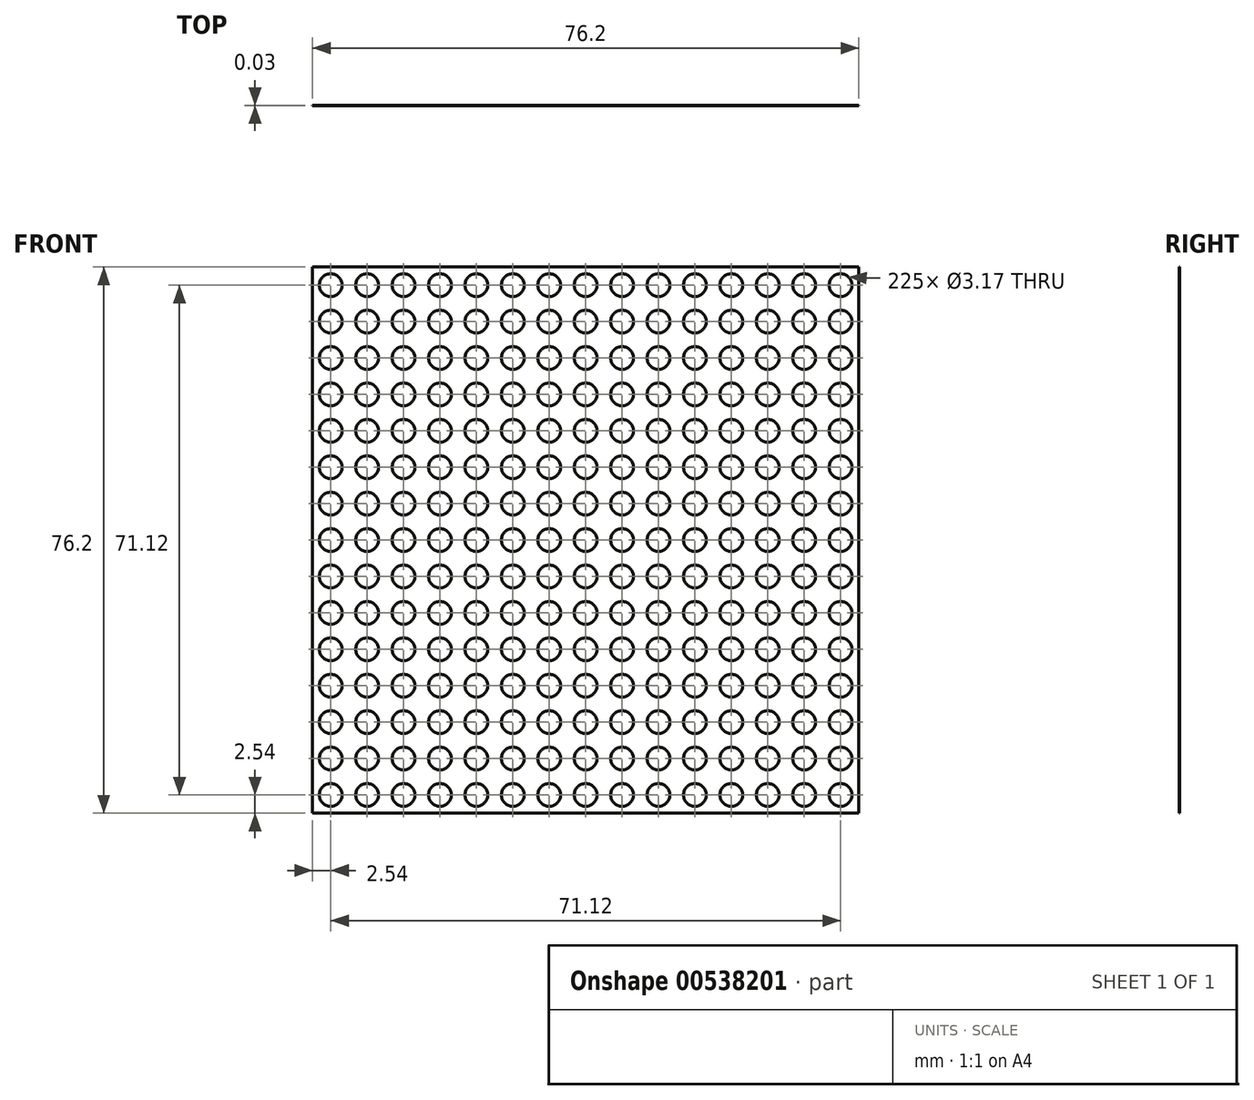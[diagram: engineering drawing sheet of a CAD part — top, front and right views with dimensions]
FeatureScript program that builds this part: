
annotation { "Feature Type Name" : "Feature", "Feature Type Description" : "" }
export const myFeature = defineFeature(function(context is Context, id is Id, definition is map)
    precondition{}
    {
        {
            var Q0;
            Q0=qCreatedBy(makeId("Front.planeOp"),FACE);
            var sketch = newSketch(context, id + "F0", { "sketchPlane" : qUnion([Q0])});
            skLineSegment(sketch, "E0", {"start": v(0, 0) * mm, "end": v(5.08, 0) * mm});
            skLineSegment(sketch, "E1", {"start": v(0, 5.08) * mm, "end": v(0, 0) * mm});
            skPoint(sketch, "E2", {"position": v(2.54, 2.54) * mm});
            skCircle(sketch, "E3", {"center": v(2.54, 2.54) * mm, "radius": 1.58 * mm});
            skPoint(sketch, "E4.MirrorP", {"position": v(7.62, 2.54) * mm});
            skCircle(sketch, "E5.MirrorC", {"center": v(7.62, 2.54) * mm, "radius": 1.58 * mm});
            skLineSegment(sketch, "E6.MirrorCS", {"start": v(10.16, 0) * mm, "end": v(5.08, 0) * mm});
            skCircle(sketch, "E7.MirrorC", {"center": v(17.78, 2.54) * mm, "radius": 1.58 * mm});
            skLineSegment(sketch, "E8.MirrorCS", {"start": v(20.32, 0) * mm, "end": v(15.24, 0) * mm});
            skCircle(sketch, "E9.MirrorC", {"center": v(12.7, 2.54) * mm, "radius": 1.58 * mm});
            skLineSegment(sketch, "E10.MirrorCS", {"start": v(10.16, 0) * mm, "end": v(15.24, 0) * mm});
            skPoint(sketch, "E11.MirrorP", {"position": v(33.02, 2.54) * mm});
            skPoint(sketch, "E12.MirrorP", {"position": v(38.1, 2.54) * mm});
            skCircle(sketch, "E13.MirrorC", {"center": v(38.1, 2.54) * mm, "radius": 1.58 * mm});
            skLineSegment(sketch, "E14.MirrorCS", {"start": v(40.64, 0) * mm, "end": v(35.56, 0) * mm});
            skLineSegment(sketch, "E15.MirrorCS", {"start": v(20.32, 0) * mm, "end": v(25.4, 0) * mm});
            skCircle(sketch, "E16.MirrorC", {"center": v(33.02, 2.54) * mm, "radius": 1.58 * mm});
            skLineSegment(sketch, "E17.MirrorCS", {"start": v(30.48, 0) * mm, "end": v(25.4, 0) * mm});
            skPoint(sketch, "E18.MirrorP", {"position": v(22.86, 2.54) * mm});
            skCircle(sketch, "E19.MirrorC", {"center": v(27.94, 2.54) * mm, "radius": 1.58 * mm});
            skCircle(sketch, "E20.MirrorC", {"center": v(22.86, 2.54) * mm, "radius": 1.58 * mm});
            skLineSegment(sketch, "E21.MirrorCS", {"start": v(30.48, 0) * mm, "end": v(35.56, 0) * mm});
            skPoint(sketch, "E22.MirrorP", {"position": v(43.18, 2.54) * mm});
            skPoint(sketch, "E23.MirrorP", {"position": v(73.66, 2.54) * mm});
            skCircle(sketch, "E24.MirrorC", {"center": v(43.18, 2.54) * mm, "radius": 1.58 * mm});
            skCircle(sketch, "E25.MirrorC", {"center": v(73.66, 2.54) * mm, "radius": 1.58 * mm});
            skCircle(sketch, "E26.MirrorC", {"center": v(63.5, 2.54) * mm, "radius": 1.58 * mm});
            skCircle(sketch, "E27.MirrorC", {"center": v(68.58, 2.54) * mm, "radius": 1.58 * mm});
            skLineSegment(sketch, "E28.MirrorCS", {"start": v(60.96, 0) * mm, "end": v(66.04, 0) * mm});
            skLineSegment(sketch, "E29.MirrorCS", {"start": v(50.8, 0) * mm, "end": v(55.88, 0) * mm});
            skPoint(sketch, "E30.MirrorP", {"position": v(58.42, 2.54) * mm});
            skLineSegment(sketch, "E31.MirrorCS", {"start": v(71.12, 0) * mm, "end": v(76.2, 0) * mm});
            skLineSegment(sketch, "E32.MirrorCS", {"start": v(60.96, 0) * mm, "end": v(55.88, 0) * mm});
            skLineSegment(sketch, "E33.MirrorCS", {"start": v(50.8, 0) * mm, "end": v(45.72, 0) * mm});
            skCircle(sketch, "E34.MirrorC", {"center": v(53.34, 2.54) * mm, "radius": 1.58 * mm});
            skLineSegment(sketch, "E35.MirrorCS", {"start": v(71.12, 0) * mm, "end": v(66.04, 0) * mm});
            skLineSegment(sketch, "E36.MirrorCS", {"start": v(40.64, 0) * mm, "end": v(45.72, 0) * mm});
            skPoint(sketch, "E37.MirrorP", {"position": v(48.26, 2.54) * mm});
            skCircle(sketch, "E38.MirrorC", {"center": v(48.26, 2.54) * mm, "radius": 1.58 * mm});
            skCircle(sketch, "E39.MirrorC", {"center": v(58.42, 2.54) * mm, "radius": 1.58 * mm});
            skLineSegment(sketch, "E40", {"start": v(76.2, 5.08) * mm, "end": v(76.2, 0) * mm});
            skPoint(sketch, "E41.MirrorP", {"position": v(12.7, 7.62) * mm});
            skCircle(sketch, "E42.MirrorC", {"center": v(53.34, 7.62) * mm, "radius": 1.58 * mm});
            skCircle(sketch, "E43.MirrorC", {"center": v(63.5, 7.62) * mm, "radius": 1.58 * mm});
            skCircle(sketch, "E44.MirrorC", {"center": v(33.02, 7.62) * mm, "radius": 1.58 * mm});
            skPoint(sketch, "E45.MirrorP", {"position": v(68.58, 7.62) * mm});
            skPoint(sketch, "E46.MirrorP", {"position": v(38.1, 7.62) * mm});
            skPoint(sketch, "E47.MirrorP", {"position": v(22.86, 7.62) * mm});
            skPoint(sketch, "E48.MirrorP", {"position": v(73.66, 7.62) * mm});
            skLineSegment(sketch, "E49.MirrorCS", {"start": v(76.2, 5.08) * mm, "end": v(76.2, 10.16) * mm});
            skCircle(sketch, "E50.MirrorC", {"center": v(48.26, 7.62) * mm, "radius": 1.58 * mm});
            skCircle(sketch, "E51.MirrorC", {"center": v(58.42, 7.62) * mm, "radius": 1.58 * mm});
            skCircle(sketch, "E52.MirrorC", {"center": v(68.58, 7.62) * mm, "radius": 1.58 * mm});
            skCircle(sketch, "E53.MirrorC", {"center": v(22.86, 7.62) * mm, "radius": 1.58 * mm});
            skCircle(sketch, "E54.MirrorC", {"center": v(27.94, 7.62) * mm, "radius": 1.58 * mm});
            skCircle(sketch, "E55.MirrorC", {"center": v(38.1, 7.62) * mm, "radius": 1.58 * mm});
            skPoint(sketch, "E56.MirrorP", {"position": v(17.78, 7.62) * mm});
            skCircle(sketch, "E57.MirrorC", {"center": v(73.66, 7.62) * mm, "radius": 1.58 * mm});
            skPoint(sketch, "E58.MirrorP", {"position": v(7.62, 7.62) * mm});
            skPoint(sketch, "E59.MirrorP", {"position": v(43.18, 7.62) * mm});
            skCircle(sketch, "E60.MirrorC", {"center": v(43.18, 7.62) * mm, "radius": 1.58 * mm});
            skCircle(sketch, "E61.MirrorC", {"center": v(12.7, 7.62) * mm, "radius": 1.58 * mm});
            skCircle(sketch, "E62.MirrorC", {"center": v(17.78, 7.62) * mm, "radius": 1.58 * mm});
            skPoint(sketch, "E63.MirrorP", {"position": v(2.54, 7.62) * mm});
            skCircle(sketch, "E64.MirrorC", {"center": v(7.62, 7.62) * mm, "radius": 1.58 * mm});
            skCircle(sketch, "E65.MirrorC", {"center": v(2.54, 7.62) * mm, "radius": 1.58 * mm});
            skLineSegment(sketch, "E66", {"start": v(0, 10.16) * mm, "end": v(0, 5.08) * mm});
            skPoint(sketch, "E67.MirrorP", {"position": v(2.54, 12.7) * mm});
            skCircle(sketch, "E68.MirrorC", {"center": v(2.54, 12.7) * mm, "radius": 1.58 * mm});
            skPoint(sketch, "E69.MirrorP", {"position": v(27.94, 17.78) * mm});
            skPoint(sketch, "E70.MirrorP", {"position": v(33.02, 17.78) * mm});
            skCircle(sketch, "E71.MirrorC", {"center": v(12.7, 12.7) * mm, "radius": 1.58 * mm});
            skPoint(sketch, "E72.MirrorP", {"position": v(2.54, 17.78) * mm});
            skLineSegment(sketch, "E73.MirrorCS", {"start": v(76.2, 15.24) * mm, "end": v(76.2, 10.16) * mm});
            skCircle(sketch, "E74.MirrorC", {"center": v(43.18, 12.7) * mm, "radius": 1.58 * mm});
            skCircle(sketch, "E75.MirrorC", {"center": v(2.54, 17.78) * mm, "radius": 1.58 * mm});
            skPoint(sketch, "E76.MirrorP", {"position": v(68.58, 17.78) * mm});
            skCircle(sketch, "E77.MirrorC", {"center": v(22.86, 12.7) * mm, "radius": 1.58 * mm});
            skPoint(sketch, "E78.MirrorP", {"position": v(58.42, 17.78) * mm});
            skPoint(sketch, "E79.MirrorP", {"position": v(73.66, 17.78) * mm});
            skPoint(sketch, "E80.MirrorP", {"position": v(73.66, 12.7) * mm});
            skLineSegment(sketch, "E81.MirrorCS", {"start": v(0, 15.24) * mm, "end": v(0, 20.32) * mm});
            skPoint(sketch, "E82.MirrorP", {"position": v(17.78, 17.78) * mm});
            skCircle(sketch, "E83.MirrorC", {"center": v(53.34, 17.78) * mm, "radius": 1.58 * mm});
            skCircle(sketch, "E84.MirrorC", {"center": v(63.5, 12.7) * mm, "radius": 1.58 * mm});
            skCircle(sketch, "E85.MirrorC", {"center": v(58.42, 17.78) * mm, "radius": 1.58 * mm});
            skPoint(sketch, "E86.MirrorP", {"position": v(7.62, 17.78) * mm});
            skCircle(sketch, "E87.MirrorC", {"center": v(63.5, 17.78) * mm, "radius": 1.58 * mm});
            skPoint(sketch, "E88.MirrorP", {"position": v(53.34, 12.7) * mm});
            skCircle(sketch, "E89.MirrorC", {"center": v(27.94, 17.78) * mm, "radius": 1.58 * mm});
            skPoint(sketch, "E90.MirrorP", {"position": v(48.26, 17.78) * mm});
            skCircle(sketch, "E91.MirrorC", {"center": v(58.42, 12.7) * mm, "radius": 1.58 * mm});
            skPoint(sketch, "E92.MirrorP", {"position": v(27.94, 12.7) * mm});
            skPoint(sketch, "E93.MirrorP", {"position": v(38.1, 17.78) * mm});
            skPoint(sketch, "E94.MirrorP", {"position": v(43.18, 17.78) * mm});
            skCircle(sketch, "E95.MirrorC", {"center": v(68.58, 12.7) * mm, "radius": 1.58 * mm});
            skCircle(sketch, "E96.MirrorC", {"center": v(68.58, 17.78) * mm, "radius": 1.58 * mm});
            skCircle(sketch, "E97.MirrorC", {"center": v(22.86, 17.78) * mm, "radius": 1.58 * mm});
            skPoint(sketch, "E98.MirrorP", {"position": v(12.7, 17.78) * mm});
            skCircle(sketch, "E99.MirrorC", {"center": v(27.94, 12.7) * mm, "radius": 1.58 * mm});
            skPoint(sketch, "E100.MirrorP", {"position": v(7.62, 12.7) * mm});
            skPoint(sketch, "E101.MirrorP", {"position": v(48.26, 12.7) * mm});
            skCircle(sketch, "E102.MirrorC", {"center": v(48.26, 17.78) * mm, "radius": 1.58 * mm});
            skPoint(sketch, "E103.MirrorP", {"position": v(33.02, 12.7) * mm});
            skCircle(sketch, "E104.MirrorC", {"center": v(33.02, 12.7) * mm, "radius": 1.58 * mm});
            skCircle(sketch, "E105.MirrorC", {"center": v(38.1, 12.7) * mm, "radius": 1.58 * mm});
            skLineSegment(sketch, "E106.MirrorCS", {"start": v(0, 10.16) * mm, "end": v(0, 15.24) * mm});
            skLineSegment(sketch, "E107.MirrorCS", {"start": v(76.2, 15.24) * mm, "end": v(76.2, 20.32) * mm});
            skCircle(sketch, "E108.MirrorC", {"center": v(7.62, 17.78) * mm, "radius": 1.58 * mm});
            skCircle(sketch, "E109.MirrorC", {"center": v(17.78, 17.78) * mm, "radius": 1.58 * mm});
            skCircle(sketch, "E110.MirrorC", {"center": v(12.7, 17.78) * mm, "radius": 1.58 * mm});
            skCircle(sketch, "E111.MirrorC", {"center": v(38.1, 17.78) * mm, "radius": 1.58 * mm});
            skCircle(sketch, "E112.MirrorC", {"center": v(33.02, 17.78) * mm, "radius": 1.58 * mm});
            skCircle(sketch, "E113.MirrorC", {"center": v(17.78, 12.7) * mm, "radius": 1.58 * mm});
            skCircle(sketch, "E114.MirrorC", {"center": v(73.66, 12.7) * mm, "radius": 1.58 * mm});
            skCircle(sketch, "E115.MirrorC", {"center": v(53.34, 12.7) * mm, "radius": 1.58 * mm});
            skCircle(sketch, "E116.MirrorC", {"center": v(43.18, 17.78) * mm, "radius": 1.58 * mm});
            skCircle(sketch, "E117.MirrorC", {"center": v(7.62, 12.7) * mm, "radius": 1.58 * mm});
            skCircle(sketch, "E118.MirrorC", {"center": v(48.26, 12.7) * mm, "radius": 1.58 * mm});
            skCircle(sketch, "E119.MirrorC", {"center": v(73.66, 17.78) * mm, "radius": 1.58 * mm});
            skCircle(sketch, "E120.MirrorC", {"center": v(17.78, 33.02) * mm, "radius": 1.58 * mm});
            skPoint(sketch, "E121.MirrorP", {"position": v(63.5, 38.1) * mm});
            skCircle(sketch, "E122.MirrorC", {"center": v(63.5, 38.1) * mm, "radius": 1.58 * mm});
            skCircle(sketch, "E123.MirrorC", {"center": v(63.5, 22.86) * mm, "radius": 1.58 * mm});
            skCircle(sketch, "E124.MirrorC", {"center": v(68.58, 33.02) * mm, "radius": 1.58 * mm});
            skPoint(sketch, "E125.MirrorP", {"position": v(27.94, 38.1) * mm});
            skPoint(sketch, "E126.MirrorP", {"position": v(17.78, 27.94) * mm});
            skCircle(sketch, "E127.MirrorC", {"center": v(12.7, 38.1) * mm, "radius": 1.58 * mm});
            skLineSegment(sketch, "E128.MirrorCS", {"start": v(76.2, 35.56) * mm, "end": v(76.2, 40.64) * mm});
            skCircle(sketch, "E129.MirrorC", {"center": v(38.1, 33.02) * mm, "radius": 1.58 * mm});
            skCircle(sketch, "E130.MirrorC", {"center": v(33.02, 27.94) * mm, "radius": 1.58 * mm});
            skCircle(sketch, "E131.MirrorC", {"center": v(53.34, 38.1) * mm, "radius": 1.58 * mm});
            skPoint(sketch, "E132.MirrorP", {"position": v(58.42, 33.02) * mm});
            skCircle(sketch, "E133.MirrorC", {"center": v(27.94, 33.02) * mm, "radius": 1.58 * mm});
            skPoint(sketch, "E134.MirrorP", {"position": v(7.62, 38.1) * mm});
            skCircle(sketch, "E135.MirrorC", {"center": v(63.5, 27.94) * mm, "radius": 1.58 * mm});
            skPoint(sketch, "E136.MirrorP", {"position": v(68.58, 38.1) * mm});
            skCircle(sketch, "E137.MirrorC", {"center": v(17.78, 38.1) * mm, "radius": 1.58 * mm});
            skCircle(sketch, "E138.MirrorC", {"center": v(33.02, 22.86) * mm, "radius": 1.58 * mm});
            skCircle(sketch, "E139.MirrorC", {"center": v(22.86, 38.1) * mm, "radius": 1.58 * mm});
            skPoint(sketch, "E140.MirrorP", {"position": v(2.54, 22.86) * mm});
            skCircle(sketch, "E141.MirrorC", {"center": v(53.34, 27.94) * mm, "radius": 1.58 * mm});
            skCircle(sketch, "E142.MirrorC", {"center": v(27.94, 38.1) * mm, "radius": 1.58 * mm});
            skCircle(sketch, "E143.MirrorC", {"center": v(38.1, 38.1) * mm, "radius": 1.58 * mm});
            skPoint(sketch, "E144.MirrorP", {"position": v(58.42, 22.86) * mm});
            skCircle(sketch, "E145.MirrorC", {"center": v(17.78, 27.94) * mm, "radius": 1.58 * mm});
            skPoint(sketch, "E146.MirrorP", {"position": v(43.18, 22.86) * mm});
            skCircle(sketch, "E147.MirrorC", {"center": v(48.26, 33.02) * mm, "radius": 1.58 * mm});
            skCircle(sketch, "E148.MirrorC", {"center": v(73.66, 38.1) * mm, "radius": 1.58 * mm});
            skCircle(sketch, "E149.MirrorC", {"center": v(22.86, 27.94) * mm, "radius": 1.58 * mm});
            skCircle(sketch, "E150.MirrorC", {"center": v(48.26, 38.1) * mm, "radius": 1.58 * mm});
            skPoint(sketch, "E151.MirrorP", {"position": v(48.26, 27.94) * mm});
            skCircle(sketch, "E152.MirrorC", {"center": v(73.66, 33.02) * mm, "radius": 1.58 * mm});
            skLineSegment(sketch, "E153.MirrorCS", {"start": v(0, 35.56) * mm, "end": v(0, 40.64) * mm});
            skCircle(sketch, "E154.MirrorC", {"center": v(2.54, 38.1) * mm, "radius": 1.58 * mm});
            skCircle(sketch, "E155.MirrorC", {"center": v(7.62, 38.1) * mm, "radius": 1.58 * mm});
            skCircle(sketch, "E156.MirrorC", {"center": v(53.34, 22.86) * mm, "radius": 1.58 * mm});
            skPoint(sketch, "E157.MirrorP", {"position": v(7.62, 33.02) * mm});
            skCircle(sketch, "E158.MirrorC", {"center": v(33.02, 38.1) * mm, "radius": 1.58 * mm});
            skPoint(sketch, "E159.MirrorP", {"position": v(17.78, 22.86) * mm});
            skCircle(sketch, "E160.MirrorC", {"center": v(12.7, 33.02) * mm, "radius": 1.58 * mm});
            skLineSegment(sketch, "E161.MirrorCS", {"start": v(0, 25.4) * mm, "end": v(0, 20.32) * mm});
            skCircle(sketch, "E162.MirrorC", {"center": v(58.42, 22.86) * mm, "radius": 1.58 * mm});
            skPoint(sketch, "E163.MirrorP", {"position": v(12.7, 27.94) * mm});
            skPoint(sketch, "E164.MirrorP", {"position": v(68.58, 22.86) * mm});
            skPoint(sketch, "E165.MirrorP", {"position": v(58.42, 27.94) * mm});
            skLineSegment(sketch, "E166.MirrorCS", {"start": v(0, 30.48) * mm, "end": v(0, 35.56) * mm});
            skCircle(sketch, "E167.MirrorC", {"center": v(58.42, 27.94) * mm, "radius": 1.58 * mm});
            skPoint(sketch, "E168.MirrorP", {"position": v(38.1, 22.86) * mm});
            skPoint(sketch, "E169.MirrorP", {"position": v(22.86, 33.02) * mm});
            skPoint(sketch, "E170.MirrorP", {"position": v(27.94, 27.94) * mm});
            skCircle(sketch, "E171.MirrorC", {"center": v(38.1, 22.86) * mm, "radius": 1.58 * mm});
            skLineSegment(sketch, "E172.MirrorCS", {"start": v(76.2, 35.56) * mm, "end": v(76.2, 30.48) * mm});
            skCircle(sketch, "E173.MirrorC", {"center": v(43.18, 22.86) * mm, "radius": 1.58 * mm});
            skCircle(sketch, "E174.MirrorC", {"center": v(12.7, 22.86) * mm, "radius": 1.58 * mm});
            skLineSegment(sketch, "E175.MirrorCS", {"start": v(76.2, 25.4) * mm, "end": v(76.2, 20.32) * mm});
            skCircle(sketch, "E176.MirrorC", {"center": v(68.58, 27.94) * mm, "radius": 1.58 * mm});
            skCircle(sketch, "E177.MirrorC", {"center": v(2.54, 27.94) * mm, "radius": 1.58 * mm});
            skCircle(sketch, "E178.MirrorC", {"center": v(27.94, 27.94) * mm, "radius": 1.58 * mm});
            skCircle(sketch, "E179.MirrorC", {"center": v(7.62, 33.02) * mm, "radius": 1.58 * mm});
            skPoint(sketch, "E180.MirrorP", {"position": v(2.54, 33.02) * mm});
            skPoint(sketch, "E181.MirrorP", {"position": v(58.42, 38.1) * mm});
            skCircle(sketch, "E182.MirrorC", {"center": v(2.54, 22.86) * mm, "radius": 1.58 * mm});
            skPoint(sketch, "E183.MirrorP", {"position": v(73.66, 22.86) * mm});
            skCircle(sketch, "E184.MirrorC", {"center": v(33.02, 33.02) * mm, "radius": 1.58 * mm});
            skPoint(sketch, "E185.MirrorP", {"position": v(43.18, 27.94) * mm});
            skCircle(sketch, "E186.MirrorC", {"center": v(7.62, 27.94) * mm, "radius": 1.58 * mm});
            skCircle(sketch, "E187.MirrorC", {"center": v(43.18, 33.02) * mm, "radius": 1.58 * mm});
            skCircle(sketch, "E188.MirrorC", {"center": v(63.5, 33.02) * mm, "radius": 1.58 * mm});
            skPoint(sketch, "E189.MirrorP", {"position": v(27.94, 22.86) * mm});
            skCircle(sketch, "E190.MirrorC", {"center": v(12.7, 27.94) * mm, "radius": 1.58 * mm});
            skCircle(sketch, "E191.MirrorC", {"center": v(43.18, 38.1) * mm, "radius": 1.58 * mm});
            skCircle(sketch, "E192.MirrorC", {"center": v(38.1, 27.94) * mm, "radius": 1.58 * mm});
            skCircle(sketch, "E193.MirrorC", {"center": v(73.66, 27.94) * mm, "radius": 1.58 * mm});
            skCircle(sketch, "E194.MirrorC", {"center": v(53.34, 33.02) * mm, "radius": 1.58 * mm});
            skCircle(sketch, "E195.MirrorC", {"center": v(22.86, 33.02) * mm, "radius": 1.58 * mm});
            skPoint(sketch, "E196.MirrorP", {"position": v(22.86, 22.86) * mm});
            skCircle(sketch, "E197.MirrorC", {"center": v(73.66, 22.86) * mm, "radius": 1.58 * mm});
            skCircle(sketch, "E198.MirrorC", {"center": v(48.26, 27.94) * mm, "radius": 1.58 * mm});
            skCircle(sketch, "E199.MirrorC", {"center": v(2.54, 33.02) * mm, "radius": 1.58 * mm});
            skCircle(sketch, "E200.MirrorC", {"center": v(27.94, 22.86) * mm, "radius": 1.58 * mm});
            skCircle(sketch, "E201.MirrorC", {"center": v(48.26, 22.86) * mm, "radius": 1.58 * mm});
            skCircle(sketch, "E202.MirrorC", {"center": v(17.78, 22.86) * mm, "radius": 1.58 * mm});
            skCircle(sketch, "E203.MirrorC", {"center": v(58.42, 38.1) * mm, "radius": 1.58 * mm});
            skCircle(sketch, "E204.MirrorC", {"center": v(58.42, 33.02) * mm, "radius": 1.58 * mm});
            skCircle(sketch, "E205.MirrorC", {"center": v(43.18, 27.94) * mm, "radius": 1.58 * mm});
            skCircle(sketch, "E206.MirrorC", {"center": v(22.86, 22.86) * mm, "radius": 1.58 * mm});
            skCircle(sketch, "E207.MirrorC", {"center": v(7.62, 22.86) * mm, "radius": 1.58 * mm});
            skCircle(sketch, "E208.MirrorC", {"center": v(68.58, 38.1) * mm, "radius": 1.58 * mm});
            skLineSegment(sketch, "E209.MirrorCS", {"start": v(76.2, 25.4) * mm, "end": v(76.2, 30.48) * mm});
            skCircle(sketch, "E210.MirrorC", {"center": v(68.58, 22.86) * mm, "radius": 1.58 * mm});
            skLineSegment(sketch, "E211.MirrorCS", {"start": v(0, 30.48) * mm, "end": v(0, 25.4) * mm});
            skCircle(sketch, "E212.MirrorC", {"center": v(63.5, 53.34) * mm, "radius": 1.58 * mm});
            skCircle(sketch, "E213.MirrorC", {"center": v(27.94, 58.42) * mm, "radius": 1.58 * mm});
            skCircle(sketch, "E214.MirrorC", {"center": v(7.62, 58.42) * mm, "radius": 1.58 * mm});
            skCircle(sketch, "E215.MirrorC", {"center": v(27.94, 68.58) * mm, "radius": 1.58 * mm});
            skCircle(sketch, "E216.MirrorC", {"center": v(58.42, 53.34) * mm, "radius": 1.58 * mm});
            skCircle(sketch, "E217.MirrorC", {"center": v(68.58, 68.58) * mm, "radius": 1.58 * mm});
            skCircle(sketch, "E218.MirrorC", {"center": v(2.54, 68.58) * mm, "radius": 1.58 * mm});
            skCircle(sketch, "E219.MirrorC", {"center": v(58.42, 68.58) * mm, "radius": 1.58 * mm});
            skCircle(sketch, "E220.MirrorC", {"center": v(33.02, 53.34) * mm, "radius": 1.58 * mm});
            skCircle(sketch, "E221.MirrorC", {"center": v(48.26, 68.58) * mm, "radius": 1.58 * mm});
            skCircle(sketch, "E222.MirrorC", {"center": v(17.78, 73.66) * mm, "radius": 1.58 * mm});
            skCircle(sketch, "E223.MirrorC", {"center": v(17.78, 53.34) * mm, "radius": 1.58 * mm});
            skCircle(sketch, "E224.MirrorC", {"center": v(27.94, 63.5) * mm, "radius": 1.58 * mm});
            skCircle(sketch, "E225.MirrorC", {"center": v(38.1, 48.26) * mm, "radius": 1.58 * mm});
            skCircle(sketch, "E226.MirrorC", {"center": v(7.62, 68.58) * mm, "radius": 1.58 * mm});
            skCircle(sketch, "E227.MirrorC", {"center": v(22.86, 63.5) * mm, "radius": 1.58 * mm});
            skCircle(sketch, "E228.MirrorC", {"center": v(22.86, 53.34) * mm, "radius": 1.58 * mm});
            skCircle(sketch, "E229.MirrorC", {"center": v(68.58, 63.5) * mm, "radius": 1.58 * mm});
            skCircle(sketch, "E230.MirrorC", {"center": v(53.34, 73.66) * mm, "radius": 1.58 * mm});
            skCircle(sketch, "E231.MirrorC", {"center": v(38.1, 63.5) * mm, "radius": 1.58 * mm});
            skCircle(sketch, "E232.MirrorC", {"center": v(63.5, 73.66) * mm, "radius": 1.58 * mm});
            skCircle(sketch, "E233.MirrorC", {"center": v(12.7, 58.42) * mm, "radius": 1.58 * mm});
            skCircle(sketch, "E234.MirrorC", {"center": v(27.94, 48.26) * mm, "radius": 1.58 * mm});
            skCircle(sketch, "E235.MirrorC", {"center": v(53.34, 48.26) * mm, "radius": 1.58 * mm});
            skCircle(sketch, "E236.MirrorC", {"center": v(17.78, 68.58) * mm, "radius": 1.58 * mm});
            skCircle(sketch, "E237.MirrorC", {"center": v(63.5, 48.26) * mm, "radius": 1.58 * mm});
            skCircle(sketch, "E238.MirrorC", {"center": v(43.18, 73.66) * mm, "radius": 1.58 * mm});
            skCircle(sketch, "E239.MirrorC", {"center": v(2.54, 43.18) * mm, "radius": 1.58 * mm});
            skCircle(sketch, "E240.MirrorC", {"center": v(12.7, 53.34) * mm, "radius": 1.58 * mm});
            skCircle(sketch, "E241.MirrorC", {"center": v(33.02, 63.5) * mm, "radius": 1.58 * mm});
            skCircle(sketch, "E242.MirrorC", {"center": v(38.1, 58.42) * mm, "radius": 1.58 * mm});
            skCircle(sketch, "E243.MirrorC", {"center": v(48.26, 48.26) * mm, "radius": 1.58 * mm});
            skCircle(sketch, "E244.MirrorC", {"center": v(73.66, 63.5) * mm, "radius": 1.58 * mm});
            skCircle(sketch, "E245.MirrorC", {"center": v(48.26, 63.5) * mm, "radius": 1.58 * mm});
            skCircle(sketch, "E246.MirrorC", {"center": v(12.7, 68.58) * mm, "radius": 1.58 * mm});
            skCircle(sketch, "E247.MirrorC", {"center": v(63.5, 68.58) * mm, "radius": 1.58 * mm});
            skCircle(sketch, "E248.MirrorC", {"center": v(7.62, 53.34) * mm, "radius": 1.58 * mm});
            skCircle(sketch, "E249.MirrorC", {"center": v(38.1, 73.66) * mm, "radius": 1.58 * mm});
            skCircle(sketch, "E250.MirrorC", {"center": v(43.18, 58.42) * mm, "radius": 1.58 * mm});
            skCircle(sketch, "E251.MirrorC", {"center": v(73.66, 48.26) * mm, "radius": 1.58 * mm});
            skCircle(sketch, "E252.MirrorC", {"center": v(53.34, 43.18) * mm, "radius": 1.58 * mm});
            skCircle(sketch, "E253.MirrorC", {"center": v(58.42, 58.42) * mm, "radius": 1.58 * mm});
            skCircle(sketch, "E254.MirrorC", {"center": v(22.86, 58.42) * mm, "radius": 1.58 * mm});
            skCircle(sketch, "E255.MirrorC", {"center": v(12.7, 63.5) * mm, "radius": 1.58 * mm});
            skCircle(sketch, "E256.MirrorC", {"center": v(33.02, 73.66) * mm, "radius": 1.58 * mm});
            skCircle(sketch, "E257.MirrorC", {"center": v(48.26, 43.18) * mm, "radius": 1.58 * mm});
            skCircle(sketch, "E258.MirrorC", {"center": v(43.18, 63.5) * mm, "radius": 1.58 * mm});
            skCircle(sketch, "E259.MirrorC", {"center": v(43.18, 43.18) * mm, "radius": 1.58 * mm});
            skCircle(sketch, "E260.MirrorC", {"center": v(7.62, 73.66) * mm, "radius": 1.58 * mm});
            skCircle(sketch, "E261.MirrorC", {"center": v(53.34, 68.58) * mm, "radius": 1.58 * mm});
            skCircle(sketch, "E262.MirrorC", {"center": v(58.42, 43.18) * mm, "radius": 1.58 * mm});
            skCircle(sketch, "E263.MirrorC", {"center": v(12.7, 73.66) * mm, "radius": 1.58 * mm});
            skCircle(sketch, "E264.MirrorC", {"center": v(73.66, 53.34) * mm, "radius": 1.58 * mm});
            skCircle(sketch, "E265.MirrorC", {"center": v(43.18, 48.26) * mm, "radius": 1.58 * mm});
            skCircle(sketch, "E266.MirrorC", {"center": v(58.42, 48.26) * mm, "radius": 1.58 * mm});
            skCircle(sketch, "E267.MirrorC", {"center": v(48.26, 58.42) * mm, "radius": 1.58 * mm});
            skCircle(sketch, "E268.MirrorC", {"center": v(43.18, 53.34) * mm, "radius": 1.58 * mm});
            skCircle(sketch, "E269.MirrorC", {"center": v(73.66, 68.58) * mm, "radius": 1.58 * mm});
            skCircle(sketch, "E270.MirrorC", {"center": v(38.1, 53.34) * mm, "radius": 1.58 * mm});
            skCircle(sketch, "E271.MirrorC", {"center": v(2.54, 73.66) * mm, "radius": 1.58 * mm});
            skCircle(sketch, "E272.MirrorC", {"center": v(73.66, 43.18) * mm, "radius": 1.58 * mm});
            skCircle(sketch, "E273.MirrorC", {"center": v(58.42, 63.5) * mm, "radius": 1.58 * mm});
            skCircle(sketch, "E274.MirrorC", {"center": v(17.78, 58.42) * mm, "radius": 1.58 * mm});
            skCircle(sketch, "E275.MirrorC", {"center": v(12.7, 43.18) * mm, "radius": 1.58 * mm});
            skCircle(sketch, "E276.MirrorC", {"center": v(63.5, 63.5) * mm, "radius": 1.58 * mm});
            skCircle(sketch, "E277.MirrorC", {"center": v(73.66, 73.66) * mm, "radius": 1.58 * mm});
            skCircle(sketch, "E278.MirrorC", {"center": v(33.02, 48.26) * mm, "radius": 1.58 * mm});
            skCircle(sketch, "E279.MirrorC", {"center": v(2.54, 48.26) * mm, "radius": 1.58 * mm});
            skCircle(sketch, "E280.MirrorC", {"center": v(17.78, 63.5) * mm, "radius": 1.58 * mm});
            skCircle(sketch, "E281.MirrorC", {"center": v(68.58, 48.26) * mm, "radius": 1.58 * mm});
            skCircle(sketch, "E282.MirrorC", {"center": v(38.1, 43.18) * mm, "radius": 1.58 * mm});
            skCircle(sketch, "E283.MirrorC", {"center": v(12.7, 48.26) * mm, "radius": 1.58 * mm});
            skCircle(sketch, "E284.MirrorC", {"center": v(27.94, 73.66) * mm, "radius": 1.58 * mm});
            skCircle(sketch, "E285.MirrorC", {"center": v(53.34, 63.5) * mm, "radius": 1.58 * mm});
            skCircle(sketch, "E286.MirrorC", {"center": v(2.54, 58.42) * mm, "radius": 1.58 * mm});
            skCircle(sketch, "E287.MirrorC", {"center": v(48.26, 53.34) * mm, "radius": 1.58 * mm});
            skCircle(sketch, "E288.MirrorC", {"center": v(63.5, 58.42) * mm, "radius": 1.58 * mm});
            skCircle(sketch, "E289.MirrorC", {"center": v(7.62, 63.5) * mm, "radius": 1.58 * mm});
            skCircle(sketch, "E290.MirrorC", {"center": v(33.02, 43.18) * mm, "radius": 1.58 * mm});
            skCircle(sketch, "E291.MirrorC", {"center": v(27.94, 43.18) * mm, "radius": 1.58 * mm});
            skCircle(sketch, "E292.MirrorC", {"center": v(22.86, 73.66) * mm, "radius": 1.58 * mm});
            skCircle(sketch, "E293.MirrorC", {"center": v(53.34, 53.34) * mm, "radius": 1.58 * mm});
            skCircle(sketch, "E294.MirrorC", {"center": v(7.62, 48.26) * mm, "radius": 1.58 * mm});
            skCircle(sketch, "E295.MirrorC", {"center": v(68.58, 73.66) * mm, "radius": 1.58 * mm});
            skCircle(sketch, "E296.MirrorC", {"center": v(22.86, 68.58) * mm, "radius": 1.58 * mm});
            skCircle(sketch, "E297.MirrorC", {"center": v(63.5, 43.18) * mm, "radius": 1.58 * mm});
            skCircle(sketch, "E298.MirrorC", {"center": v(22.86, 43.18) * mm, "radius": 1.58 * mm});
            skCircle(sketch, "E299.MirrorC", {"center": v(73.66, 58.42) * mm, "radius": 1.58 * mm});
            skCircle(sketch, "E300.MirrorC", {"center": v(27.94, 53.34) * mm, "radius": 1.58 * mm});
            skCircle(sketch, "E301.MirrorC", {"center": v(2.54, 63.5) * mm, "radius": 1.58 * mm});
            skCircle(sketch, "E302.MirrorC", {"center": v(58.42, 73.66) * mm, "radius": 1.58 * mm});
            skCircle(sketch, "E303.MirrorC", {"center": v(17.78, 48.26) * mm, "radius": 1.58 * mm});
            skCircle(sketch, "E304.MirrorC", {"center": v(68.58, 58.42) * mm, "radius": 1.58 * mm});
            skCircle(sketch, "E305.MirrorC", {"center": v(33.02, 58.42) * mm, "radius": 1.58 * mm});
            skCircle(sketch, "E306.MirrorC", {"center": v(53.34, 58.42) * mm, "radius": 1.58 * mm});
            skCircle(sketch, "E307.MirrorC", {"center": v(2.54, 53.34) * mm, "radius": 1.58 * mm});
            skCircle(sketch, "E308.MirrorC", {"center": v(22.86, 48.26) * mm, "radius": 1.58 * mm});
            skCircle(sketch, "E309.MirrorC", {"center": v(48.26, 73.66) * mm, "radius": 1.58 * mm});
            skCircle(sketch, "E310.MirrorC", {"center": v(43.18, 68.58) * mm, "radius": 1.58 * mm});
            skCircle(sketch, "E311.MirrorC", {"center": v(38.1, 68.58) * mm, "radius": 1.58 * mm});
            skCircle(sketch, "E312.MirrorC", {"center": v(17.78, 43.18) * mm, "radius": 1.58 * mm});
            skCircle(sketch, "E313.MirrorC", {"center": v(7.62, 43.18) * mm, "radius": 1.58 * mm});
            skCircle(sketch, "E314.MirrorC", {"center": v(68.58, 53.34) * mm, "radius": 1.58 * mm});
            skCircle(sketch, "E315.MirrorC", {"center": v(33.02, 68.58) * mm, "radius": 1.58 * mm});
            skCircle(sketch, "E316.MirrorC", {"center": v(68.58, 43.18) * mm, "radius": 1.58 * mm});
            skLineSegment(sketch, "E317.MirrorCS", {"start": v(0, 71.12) * mm, "end": v(0, 76.2) * mm});
            skLineSegment(sketch, "E318.MirrorCS", {"start": v(0, 50.8) * mm, "end": v(0, 45.72) * mm});
            skLineSegment(sketch, "E319.MirrorCS", {"start": v(76.2, 55.88) * mm, "end": v(76.2, 60.96) * mm});
            skLineSegment(sketch, "E320.MirrorCS", {"start": v(76.2, 45.72) * mm, "end": v(76.2, 40.64) * mm});
            skLineSegment(sketch, "E321.MirrorCS", {"start": v(0, 45.72) * mm, "end": v(0, 40.64) * mm});
            skLineSegment(sketch, "E322.MirrorCS", {"start": v(76.2, 45.72) * mm, "end": v(76.2, 50.8) * mm});
            skLineSegment(sketch, "E323.MirrorCS", {"start": v(0, 55.88) * mm, "end": v(0, 60.96) * mm});
            skLineSegment(sketch, "E324.MirrorCS", {"start": v(0, 66.04) * mm, "end": v(0, 60.96) * mm});
            skLineSegment(sketch, "E325.MirrorCS", {"start": v(76.2, 66.04) * mm, "end": v(76.2, 60.96) * mm});
            skLineSegment(sketch, "E326.MirrorCS", {"start": v(0, 50.8) * mm, "end": v(0, 55.88) * mm});
            skLineSegment(sketch, "E327.MirrorCS", {"start": v(0, 71.12) * mm, "end": v(0, 66.04) * mm});
            skLineSegment(sketch, "E328.MirrorCS", {"start": v(76.2, 55.88) * mm, "end": v(76.2, 50.8) * mm});
            skLineSegment(sketch, "E329.MirrorCS", {"start": v(76.2, 76.2) * mm, "end": v(76.2, 71.12) * mm});
            skLineSegment(sketch, "E330.MirrorCS", {"start": v(76.2, 66.04) * mm, "end": v(76.2, 71.12) * mm});
            skLineSegment(sketch, "E331", {"start": v(0, 76.2) * mm, "end": v(76.2, 76.2) * mm});
            skSolve(sketch);
        }
        {
            var Q0;
            Q0 = qSketchRegion(id + "F0", true);
            extrude(context, id + "F1", {"entities" : qUnion([Q0]), "depth" : 0.03 * mm, "offsetDistance" : 25.4 * mm});
        }
    });
